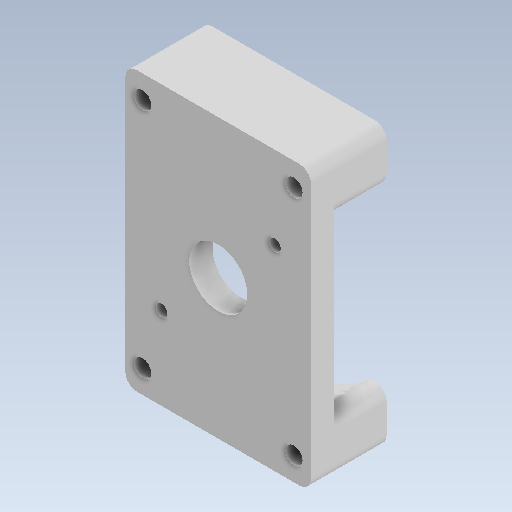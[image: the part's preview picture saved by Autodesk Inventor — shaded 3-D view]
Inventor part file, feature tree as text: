
AUTODESK INVENTOR PART (.ipt)
format: ipt  version: 2020 (Build 240168000, 168)  size: 158,208 bytes
history: native  units: in
note: dims shown in document units (in); Inventor stores cm internally (conversion verified against a paired STEP export)
features: reference x15, other x5, sketch x2, extrude x2, plane x1, fillet x1
ambient origin geometry x8: Origin, YZ Plane, XZ Plane, XY Plane, X Axis, Y Axis, Z Axis, Center Point
bodies: Solid1 (feature_tree)
feature tree (26):
  sketch  "Sketch1"  dims[d0=1.0in d1=0.0in d2=0.625in]
  plane  "Work Plane1"
  extrude  "Extrusion1"  Depth=0.625in
  extrude  "Extrusion2"  Depth=0.125in
  fillet  "Fillet1"  [1 undecoded]
  reference  "Reference1"
  reference  "Reference2"
  reference  "Reference3"
  reference  "Reference4"
  reference  "Reference5"
  reference  "Reference6"
  reference  "Reference7"
  reference  "Reference8"
  reference  "Reference9"
  reference  "Reference10"
  reference  "Reference11"
  sketch  "Sketch2"  dims[d3=0.25in d4=0.0in d5=0.125in]
  reference  "Reference12"
  reference  "Reference13"
  reference  "Reference14"
  reference  "Reference15"
  other  "<userpath>\Desktop\PnP Machine\PnP Machine.iam"
  other  "PnP Machine.iam"
  other  "Encoder Mount Y:1"
  other  "47065T605_ALUMINUM T-SLOTTED FRAMING EXTRUSION:2"
  other  "CUI_DEVICES_AMT132Q-4096-1270:1"
note: 1 required parameter value undecoded (feature->parameter linkage not recoverable at this tier; creation-order binding heuristic only, values carry confidence <= 0.55)
